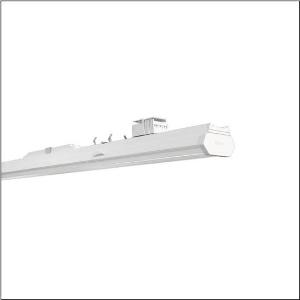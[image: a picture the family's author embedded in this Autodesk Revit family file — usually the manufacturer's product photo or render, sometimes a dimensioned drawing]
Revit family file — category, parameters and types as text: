
# Revit family: licross_21_protected_mo_52td11dn4a5g
name_source: partatom
category: Lighting Fixtures
units: mm (PartAtom-declared; Revit-internal decimal feet)

## family parameters
Cut with Voids When Loaded = No
Host = Face
Light Source = No
Part Type = Normal
Room Calculation Point = No
Round Connector Dimension = Use Diameter
Shared = No

## types (1)
- --- (1 x LED, 10650 lm, 62 W, 4000K)
    Apparent Load = 62 VA
    CIE Flux Codes = 83 94 98 100 100
    Color Rendering = 80
    Color Temperature = 4000K
    Default Elevation = 1800 mm
    Description = Licross 21 Protected MO, luminaire insert, of sheet steel, galvanised, coil coated, white, length: 1.500mm, width: 90mm, height: 103mm, LED rated luminous flux: 10.650lm, light colour: 840, SDCM (Standard Deviation of Colour Matching)MacAdam ≤ 3 SDCM (initial), control gear: DALI 2, with plug, 5-pole, with phase selection, mains connection: 220..240V, AC, 50/60Hz, rated input power: 62W, internal wiring halogen-free, primary light control with lens, of plastic, primary optical cover: cover, of PMMA, light emission: direct distribution, primary light characteristic: symmetric, protection rating (complete): IP54, insulation class (complete): insulation class I (protective earthing), certification: CE, ENEC, VDE, UKCA, protection symbol: D if used in an environment with non-conductive dust loads with corresponding accessories, impact resistance: IK06, permissible ambient temperature for indoor applications: -25..+35°C, corresponds to IFS (International Featured Standards) requirements for safety and quality in the food industry, reducing of maximum allowable ambient temperature of 5°C with ceiling mounting, LABS conformity tested according to VDMA 24364:2018-05, The light source and the operating device comply with the requirements of the Ecodesign Regulation (EU) 2019/2020 and are replaceable in accordance with this regulation, packaging unit: 1 piece
    Height = 92 mm
    Lamp = 1 x LED
    Lamp Light Flux = 10650 lm
    Lamp Power = 62 W
    Lamp count = 1
    Length = 1500 mm
    Luminous efficacy = 172 lm/W
    Manufacturer = Siteco
    ModVariant = No
    Model = 52TD11DN4A5G
    Mounting Place = Ceiling
    Mounting Type = Pendant
    Number of Poles = 1
    OnlyDefault = Yes
    Power Factor = 1
    Product Name = Licross 21 Protected MO
    Product group = luminaire insert | ceiling pendant
    ProductGroupID = 901
    Protection Class = Protection class I
    Protection Degree = IP 54
    RLX_Detail_Level = 1
    RLX_Emergency_Light_Flux = 0 lm
    RLX_Emergency_Type = 0
    RLX_Emergency_Type_DB = No
    RlxData = <blob elided: 24373 chars, md5=da0b10ae>
    Socket = socket
    Standby Power = 0 W
    System Light Flux = 10650 lm
    System Power = 62 W
    Type Comments = factory setting: luminous flux: 100 % | dim-lin: 254 | 418 mA
    Type Image = l_1256148.jpg
    URL = http://relux.com
    VarID = @adj_130023
    Voltage = 0 V
    Weight = 0.00 kg
    Width = 88 mm

## geometry (parser evidence)
native form markers: Blend x4, Sweep x11
no freeform markers — native parametric forms only
